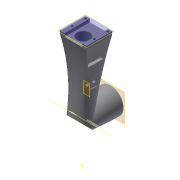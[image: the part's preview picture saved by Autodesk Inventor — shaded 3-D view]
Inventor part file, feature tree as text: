
AUTODESK INVENTOR PART (.ipt)
format: ipt  version: 2019.4 (Build 234330000, 330)  size: 427,520 bytes
history: native  units: mm
features: sketch x14, reference x12, extrude x9, other x7, plane x6, projected_geometry x3, loft x2
ambient origin geometry x8: Origin, YZ Plane, XZ Plane, XY Plane, X Axis, Y Axis, Z Axis, Center Point
bodies: Solid1 (feature_tree)
feature tree (53):
  plane  "Work Plane1"
  extrude  "Extrusion1"  Depth=4.0mm
  sketch  "Sketch2"  dims[d2=1.5mm d3=1.5mm]
  plane  "Work Plane2"
  loft  "Loft1"
  sketch  "Sketch4"  dims[d6=3.0mm d7=0.0mm d8=20.0mm]
  plane  "Work Plane3"
  loft  "Loft2"
  plane  "Work Plane4"
  extrude  "Extrusion2"  Depth=20.0mm
  extrude  "Extrusion3"  Depth=3.0mm TaperAngle=0.0deg
  extrude  "Extrusion4"  Depth=3.0mm TaperAngle=0.0deg
  extrude  "Extrusion5"  Depth=22.0mm
  sketch  "Sketch10"  dims[d31=5.0mm d32=0.0mm d35=0.0mm d36=90.0deg]
  plane  "Work Plane5"
  extrude  "Extrusion6"  Depth=20.0mm
  sketch  "Sketch11"  dims[d37=10.0mm d38=90.0deg d47=10.0mm d48=13.962634mm d49=0.0mm d50=90.0deg]
  plane  "Work Plane6"
  extrude  "Extrusion7"  TaperAngle=60.0deg  [1 undecoded]
  extrude  "Extrusion8"  TaperAngle=0.0deg  [1 undecoded]
  extrude  "Extrusion9"  Depth=10.0mm TaperAngle=0.0deg
  sketch  "Sketch1"  dims[d0=4.0mm d1=4.0mm]
  reference  "Reference1"
  projected_geometry  "Projected Loop1"
  projected_geometry  "Projected Loop2"
  sketch  "Sketch3"  dims[d4=1.5mm d5=1.5mm]
  reference  "Reference2"
  projected_geometry  "Projected Loop3"
  sketch  "Sketch5"  dims[d17=-3.0mm d18=3.0mm d19=0.0mm]
  reference  "Reference3"
  reference  "Reference4"
  sketch  "Sketch6"  dims[d20=16.0mm d21=3.0mm d22=0.0mm]
  reference  "Reference5"
  sketch  "Sketch7"  dims[d23=3.0mm d24=0.0mm d25=22.0mm]
  reference  "Reference6"
  sketch  "Sketch8"  dims[d26=5.0mm d27=0.0mm d28=20.0mm]
  sketch  "Sketch9"  dims[d29=60.0deg d30=60.0deg]
  reference  "Reference7"
  reference  "Reference8"
  sketch  "Sketch12"  dims[d51=5.0mm d52=0.0mm]
  reference  "Reference14"
  reference  "Reference15"
  sketch  "Sketch13"  dims[d53=5.0mm d54=0.0mm]
  sketch  "Sketch14"  dims[d55=1.5mm d56=15.0mm d57=3.0mm d58=14.0mm d59=5.0mm d60=0.0mm]
  reference  "Reference17"
  reference  "Reference18"
  other  "Assembly_Opentrons_Autofocus_v2.iam"
  other  "00_RasPi_Camera:1"
  other  "00_COMAR_Mirror_10mm:1"
  other  "00_objectivelens_10x:1"
  other  "07_OPENTRONS_Autofocus_objectivemount_v0:1"
  other  "01_Slide_camera_v1:1"
  other  "01_Slide_camera_flexure_v1:1"
note: 2 required parameter values undecoded (feature->parameter linkage not recoverable at this tier; creation-order binding heuristic only, values carry confidence <= 0.55)
